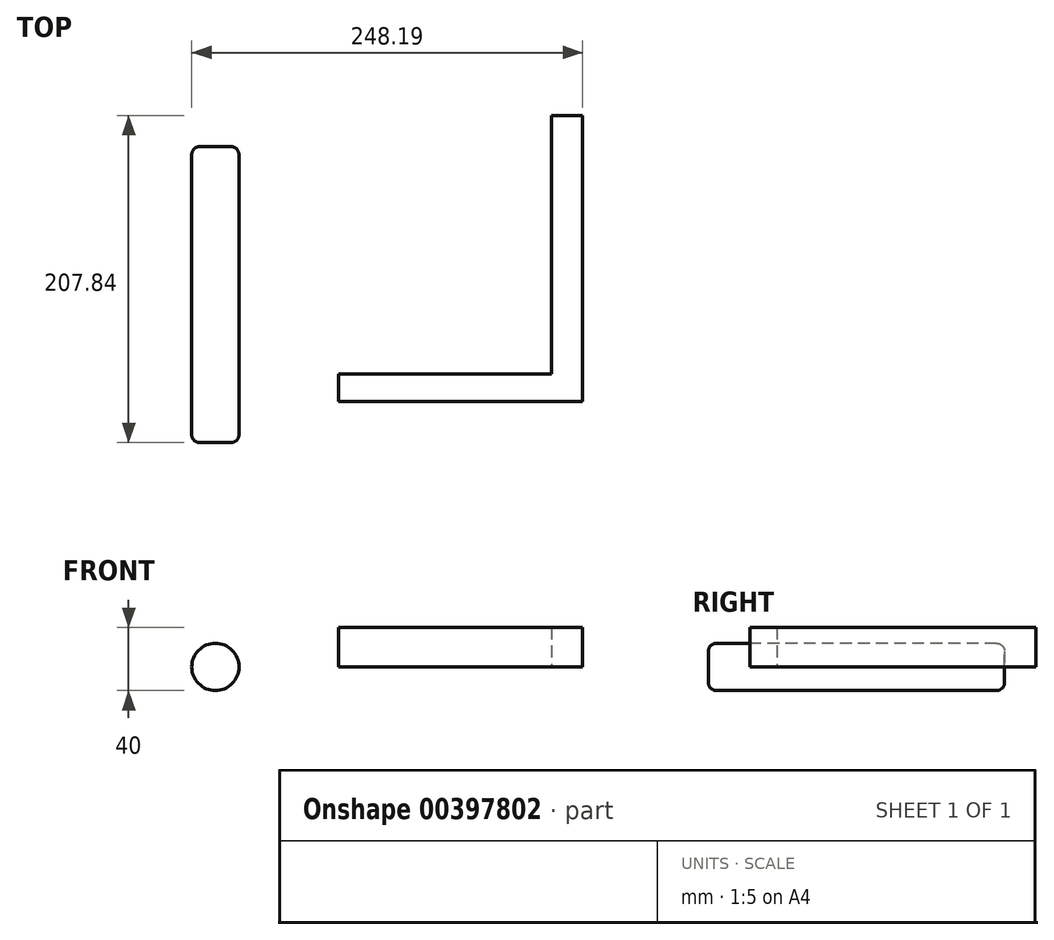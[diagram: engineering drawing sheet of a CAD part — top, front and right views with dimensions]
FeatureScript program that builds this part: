
annotation { "Feature Type Name" : "Feature", "Feature Type Description" : "" }
export const myFeature = defineFeature(function(context is Context, id is Id, definition is map)
    precondition{}
    {
        {
            var Q0;
            Q0=qCreatedBy(makeId("Front.planeOp"),FACE);
            var sketch = newSketch(context, id + "F0", { "sketchPlane" : qUnion([Q0])});
            skCircle(sketch, "E0", {"center": v(0, 0) * mm, "radius": 15 * mm});
            skSolve(sketch);
        }
        {
            var Q0;
            Q0=makeQuery(id+"F0.imprint","IMPRINT",FACE,{"disambiguationData":[TD([[makeQuery(id+"F0.imprint","IMPRINT",EDGE,{"derivedFrom":sQuery(id+"F0.wireOp",EDGE,"E0")}),1.0]])]});
            extrude(context, id + "F1", {"entities" : qUnion([Q0]), "endBound" : BoundingType.SYMMETRIC, "oppositeDirection" : true, "depth" : 188 * mm});
        }
        {
            var Q0;
            Q0=makeQuery(id+"F1.opExtrude","CAP_EDGE",EDGE,{"disambiguationData":[OSD([sQuery(id+"F0.wireOp",EDGE,"E0")])],"isStart":false});
            var Q1;
            Q1=makeQuery(id+"F1.opExtrude","CAP_EDGE",EDGE,{"disambiguationData":[OSD([sQuery(id+"F0.wireOp",EDGE,"E0")])],"isStart":true});
            fillet(context, id + "F2", {"entities" : qUnion([Q0, Q1]), "radius" : 5 * mm, "tangentPropagation" : true, "allowEdgeOverflow" : false});
        }
        {
            var Q0;
            Q0=qCreatedBy(makeId("Top.planeOp"),FACE);
            var sketch = newSketch(context, id + "F3", { "sketchPlane" : qUnion([Q0])});
            skLineSegment(sketch, "E1.bottom", {"start": v(213.39, 113.84) * mm, "end": v(233.2, 113.84) * mm});
            skLineSegment(sketch, "E1.top", {"start": v(213.39, -67.77) * mm, "end": v(233.2, -67.77) * mm});
            skLineSegment(sketch, "E1.left", {"start": v(213.39, 113.84) * mm, "end": v(213.39, -67.77) * mm});
            skLineSegment(sketch, "E1.right", {"start": v(233.2, 113.84) * mm, "end": v(233.2, -67.77) * mm});
            skLineSegment(sketch, "E2.bottom", {"start": v(213.39, -67.77) * mm, "end": v(78.37, -67.77) * mm});
            skLineSegment(sketch, "E2.top", {"start": v(213.39, -50.58) * mm, "end": v(78.37, -50.58) * mm});
            skLineSegment(sketch, "E2.left", {"start": v(213.39, -67.77) * mm, "end": v(213.39, -50.58) * mm});
            skLineSegment(sketch, "E2.right", {"start": v(78.37, -67.77) * mm, "end": v(78.37, -50.58) * mm});
            skSolve(sketch);
        }
        {
            var Q0;
            Q0=makeQuery(id+"F3.imprint","IMPRINT",FACE,{"disambiguationData":[TD([[makeQuery(id+"F3.imprint","IMPRINT",EDGE,{"derivedFrom":sQuery(id+"F3.wireOp",EDGE,"E1.bottom")}),-1.0]])]});
            var Q1;
            Q1=makeQuery(id+"F3.imprint","IMPRINT",FACE,{"disambiguationData":[TD([[makeQuery(id+"F3.imprint","IMPRINT",EDGE,{"derivedFrom":sQuery(id+"F3.wireOp",EDGE,"E2.bottom")}),-1.0]])]});
            extrude(context, id + "F4", {"entities" : qUnion([Q0, Q1]), "depth" : 25 * mm});
        }
    });
